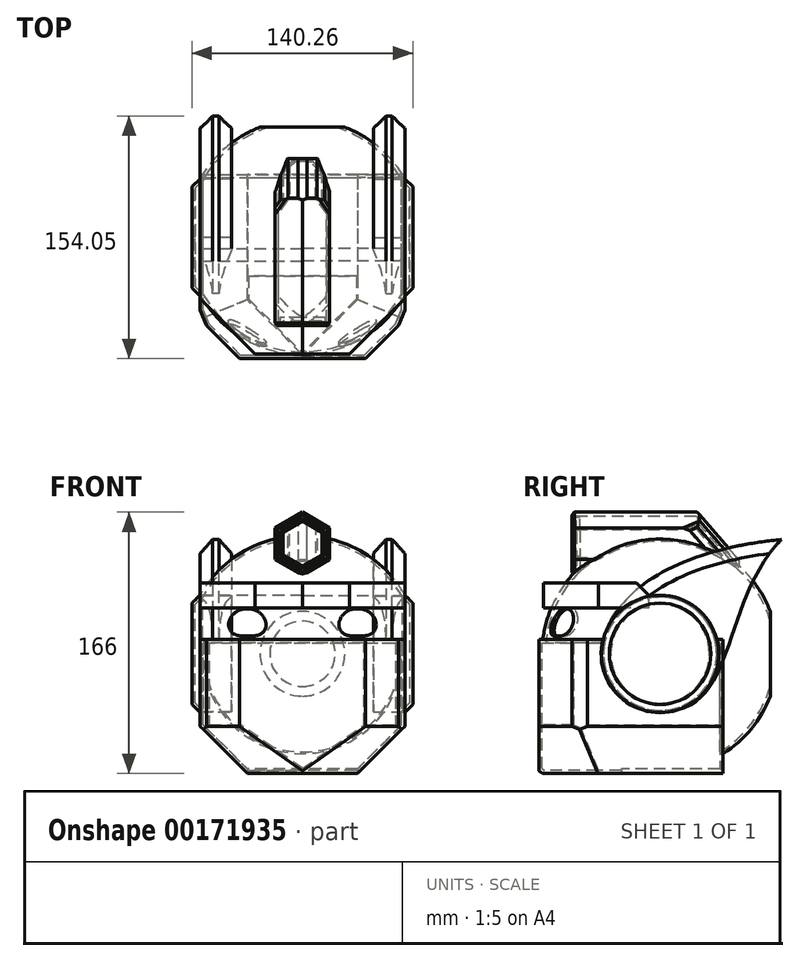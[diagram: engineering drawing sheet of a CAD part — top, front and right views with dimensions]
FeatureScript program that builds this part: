
annotation { "Feature Type Name" : "Feature", "Feature Type Description" : "" }
export const myFeature = defineFeature(function(context is Context, id is Id, definition is map)
    precondition{}
    {
        {
            var Q0;
            Q0=qCreatedBy(makeId("Top.planeOp"),FACE);
            var sketch = newSketch(context, id + "F0", { "sketchPlane" : qUnion([Q0])});
            skArc(sketch, "E0", {"start": v(0, 75) * mm, "mid": v(-75, 0) * mm, "end": v(0, -75) * mm});
            skLineSegment(sketch, "E1", {"start": v(0, 84.9) * mm, "end": v(0, -83.98) * mm});
            skSolve(sketch);
        }
        {
            var Q0;
            Q0=makeQuery(id+"F0.imprint","IMPRINT",FACE,{"disambiguationData":[TD([[makeQuery(id+"F0.imprint","IMPRINT",EDGE,{"derivedFrom":sQuery(id+"F0.wireOp",EDGE,"E0")}),1.0]])]});
            var Q1;
            Q1=sQuery(id+"F0.wireOp",EDGE,"E0");
            var Q2;
            Q2=sQuery(id+"F0.wireOp",EDGE,"E1");
            revolve(context, id + "F1", {"entities" : qUnion([Q0]), "surfaceEntities" : qUnion([Q1]), "axis" : qUnion([Q2]), "revolveType" : RevolveType.FULL});
        }
        {
            var Q0;
            Q0=qCreatedBy(makeId("Front.planeOp"),FACE);
            cPlane(context, id + "F2", {"entities" : qUnion([Q0]), "cplaneType" : CPlaneType.OFFSET, "offset" : 75 * mm, "width" : 150 * mm, "height" : 150 * mm});
        }
        {
            var Q0;
            Q0=qCreatedBy(makeId("Front.planeOp"),FACE);
            cPlane(context, id + "F3", {"entities" : qUnion([Q0]), "cplaneType" : CPlaneType.OFFSET, "offset" : 70 * mm, "oppositeDirection" : true, "width" : 150 * mm, "height" : 150 * mm});
        }
        {
            var Q0;
            Q0=qCreatedBy(id+"F3.planeOp",FACE);
            var sketch = newSketch(context, id + "F4", { "sketchPlane" : qUnion([Q0])});
            skLineSegment(sketch, "E2.bottom", {"start": v(32.42, 33.51) * mm, "end": v(-32.42, 33.51) * mm});
            skLineSegment(sketch, "E2.top", {"start": v(32.42, -33.51) * mm, "end": v(-32.42, -33.51) * mm});
            skLineSegment(sketch, "E2.left", {"start": v(32.42, 33.51) * mm, "end": v(32.42, -33.51) * mm});
            skLineSegment(sketch, "E2.right", {"start": v(-32.42, 33.51) * mm, "end": v(-32.42, -33.51) * mm});
            skPoint(sketch, "E2.middle", {"position": v(0, 0) * mm});
            skSolve(sketch);
        }
        {
            var Q0;
            Q0 = qSketchRegion(id + "F4", true);
            extrude(context, id + "F5", {"entities" : qUnion([Q0]), "operationType" : NewBodyOperationType.REMOVE, "oppositeDirection" : true, "depth" : 25 * mm});
        }
        {
            var Q0;
            Q0=qCreatedBy(id+"F2.planeOp",FACE);
            var sketch = newSketch(context, id + "F6", { "sketchPlane" : qUnion([Q0])});
            skCircle(sketch, "E3", {"center": v(-35, 20) * mm, "radius": 15 * mm});
            skLineSegment(sketch, "E4", {"start": v(-59.74, 0) * mm, "end": v(64.05, 0) * mm, "construction": true});
            skLineSegment(sketch, "E5", {"start": v(0, 51.11) * mm, "end": v(0, -49.41) * mm, "construction": true});
            skLineSegment(sketch, "E6.bottom", {"start": v(-45, 26.5) * mm, "end": v(-25, 26.5) * mm});
            skLineSegment(sketch, "E6.top", {"start": v(-45, 13.5) * mm, "end": v(-25, 13.5) * mm});
            skLineSegment(sketch, "E6.left", {"start": v(-45, 26.5) * mm, "end": v(-45, 13.5) * mm});
            skLineSegment(sketch, "E6.right", {"start": v(-25, 26.5) * mm, "end": v(-25, 13.5) * mm});
            skLineSegment(sketch, "E7.MirrorCS", {"start": v(25, 26.5) * mm, "end": v(25, 13.5) * mm});
            skLineSegment(sketch, "E8.MirrorCS", {"start": v(45, 26.5) * mm, "end": v(25, 26.5) * mm});
            skLineSegment(sketch, "E9.MirrorCS", {"start": v(45, 13.5) * mm, "end": v(25, 13.5) * mm});
            skLineSegment(sketch, "E10.MirrorCS", {"start": v(45, 26.5) * mm, "end": v(45, 13.5) * mm});
            skSolve(sketch);
        }
        {
            var Q0;
            Q0=makeQuery(id+"F6.imprint","IMPRINT",FACE,{"disambiguationData":[TD([[makeQuery(id+"F6.imprint","IMPRINT",EDGE,{"derivedFrom":sQuery(id+"F6.wireOp",EDGE,"E7.MirrorCS")}),1.0]])]});
            var Q1;
            Q1=makeQuery(id+"F6.imprint","IMPRINT",FACE,{"disambiguationData":[TD([[makeQuery(id+"F6.imprint","IMPRINT",EDGE,{"derivedFrom":sQuery(id+"F6.wireOp",EDGE,"E6.bottom")}),-1.0]])]});
            extrude(context, id + "F7", {"entities" : qUnion([Q0, Q1]), "operationType" : NewBodyOperationType.REMOVE, "oppositeDirection" : true, "depth" : 25 * mm});
        }
        {
            var Q0;
            Q0=qCreatedBy(makeId("Right.planeOp"),FACE);
            var sketch = newSketch(context, id + "F8", { "sketchPlane" : qUnion([Q0])});
            skLineSegment(sketch, "E11", {"start": v(-77, 9) * mm, "end": v(-77, -76) * mm});
            skLineSegment(sketch, "E12", {"start": v(-77, -76) * mm, "end": v(40, -76) * mm});
            skLineSegment(sketch, "E13", {"start": v(40, -76) * mm, "end": v(40, 9) * mm});
            skLineSegment(sketch, "E14", {"start": v(-77, 9) * mm, "end": v(40, 9) * mm});
            skSolve(sketch);
        }
        {
            var Q0;
            Q0 = qSketchRegion(id + "F8", true);
            extrude(context, id + "F9", {"entities" : qUnion([Q0]), "operationType" : NewBodyOperationType.ADD, "endBound" : BoundingType.SYMMETRIC, "depth" : 130 * mm});
        }
        {
            var Q0;
            Q0=qCreatedBy(makeId("Top.planeOp"),FACE);
            var sketch = newSketch(context, id + "F10", { "sketchPlane" : qUnion([Q0])});
            skLineSegment(sketch, "E15", {"start": v(0, -130) * mm, "end": v(-141.87, 0) * mm});
            skLineSegment(sketch, "E16", {"start": v(-141.87, 0) * mm, "end": v(0, 0) * mm});
            skLineSegment(sketch, "E17", {"start": v(0, 0) * mm, "end": v(0, -130) * mm});
            skLineSegment(sketch, "E18.MirrorCS", {"start": v(0, -130) * mm, "end": v(141.87, 0) * mm});
            skLineSegment(sketch, "E19.MirrorCS", {"start": v(141.87, 0) * mm, "end": v(0, 0) * mm});
            skLineSegment(sketch, "E20.bottom", {"start": v(-81.28, 0) * mm, "end": v(78.72, 0) * mm});
            skLineSegment(sketch, "E20.top", {"start": v(-81.28, -150) * mm, "end": v(78.72, -150) * mm});
            skLineSegment(sketch, "E20.left", {"start": v(-81.28, 0) * mm, "end": v(-81.28, -150) * mm});
            skLineSegment(sketch, "E20.right", {"start": v(78.72, 0) * mm, "end": v(78.72, -150) * mm});
            skLineSegment(sketch, "E21.bottom", {"start": v(-93.95, -108.92) * mm, "end": v(106.59, -108.92) * mm});
            skLineSegment(sketch, "E21.top", {"start": v(-93.95, -86.95) * mm, "end": v(106.59, -86.95) * mm});
            skLineSegment(sketch, "E21.left", {"start": v(-93.95, -108.92) * mm, "end": v(-93.95, -86.95) * mm});
            skLineSegment(sketch, "E21.right", {"start": v(106.59, -108.92) * mm, "end": v(106.59, -86.95) * mm});
            skSolve(sketch);
        }
        {
            var Q0;
            Q0=qCreatedBy(id+"F2.planeOp",FACE);
            var sketch = newSketch(context, id + "F11", { "sketchPlane" : qUnion([Q0])});
            skLineSegment(sketch, "E22.bottom", {"start": v(-79.13, 41.89) * mm, "end": v(-65.13, 41.89) * mm});
            skLineSegment(sketch, "E22.top", {"start": v(-79.13, -58.11) * mm, "end": v(-65.13, -58.11) * mm});
            skLineSegment(sketch, "E22.left", {"start": v(-79.13, 41.89) * mm, "end": v(-79.13, -58.11) * mm});
            skLineSegment(sketch, "E22.right", {"start": v(-65.13, 41.89) * mm, "end": v(-65.13, -58.11) * mm});
            skLineSegment(sketch, "E23.MirrorCS", {"start": v(65.13, 41.89) * mm, "end": v(65.13, -58.11) * mm});
            skLineSegment(sketch, "E24.MirrorCS", {"start": v(79.13, 41.89) * mm, "end": v(65.13, 41.89) * mm});
            skLineSegment(sketch, "E25.MirrorCS", {"start": v(79.13, 41.89) * mm, "end": v(79.13, -58.11) * mm});
            skLineSegment(sketch, "E26.MirrorCS", {"start": v(79.13, -58.11) * mm, "end": v(65.13, -58.11) * mm});
            skSolve(sketch);
        }
        {
            var Q0;
            Q0=makeQuery(id+"F11.imprint","IMPRINT",FACE,{"disambiguationData":[TD([[makeQuery(id+"F11.imprint","IMPRINT",EDGE,{"derivedFrom":sQuery(id+"F11.wireOp",EDGE,"E22.bottom")}),-1.0]])]});
            var Q1;
            Q1=makeQuery(id+"F11.imprint","IMPRINT",FACE,{"disambiguationData":[TD([[makeQuery(id+"F11.imprint","IMPRINT",EDGE,{"derivedFrom":sQuery(id+"F11.wireOp",EDGE,"E23.MirrorCS")}),1.0]])]});
            extrude(context, id + "F12", {"entities" : qUnion([Q0, Q1]), "operationType" : NewBodyOperationType.REMOVE, "oppositeDirection" : true, "depth" : 135.1 * mm});
        }
        {
            var Q0;
            Q0=qCreatedBy(makeId("Right.planeOp"),FACE);
            cPlane(context, id + "F13", {"entities" : qUnion([Q0]), "cplaneType" : CPlaneType.OFFSET, "offset" : 65 * mm, "width" : 150 * mm, "height" : 150 * mm});
        }
        {
            var Q0;
            {var subQ1=sQuery(id+"F10.wireOp",EDGE,"E20.top");Q0=makeQuery(id+"F10.imprint","IMPRINT",FACE,{"disambiguationData":[TD([[makeQuery(id+"F10.imprint","IMPRINT",EDGE,{"derivedFrom":subQ1}),1.0]])]});}
            extrude(context, id + "F14", {"entities" : qUnion([Q0]), "operationType" : NewBodyOperationType.REMOVE, "endBound" : BoundingType.THROUGH_ALL, "oppositeDirection" : true, "depth" : 25 * mm});
        }
        {
            var Q0;
            Q0=makeQuery(id+"F9.opExtrude","CAP_EDGE",EDGE,{"disambiguationData":[OSD([sQuery(id+"F8.wireOp",EDGE,"E11")])],"isStart":true});
            var Q1;
            Q1=makeQuery(id+"F9.opExtrude","CAP_EDGE",EDGE,{"disambiguationData":[OSD([sQuery(id+"F8.wireOp",EDGE,"E11")])],"isStart":false});
            chamfer(context, id + "F15", {"entities" : qUnion([Q0, Q1]), "width" : 25 * mm, "tangentPropagation" : true});
        }
        {
            var Q0;
            Q0=makeQuery(id+"F7.boolean.opBoolean","COPY",EDGE,{"derivedFrom":makeQuery(id+"F7.opExtrude","SWEPT_EDGE",EDGE,{"disambiguationData":[OSD([sQuery(id+"F6.wireOp",EDGE,"E7.MirrorCS"),sQuery(id+"F6.wireOp",EDGE,"E8.MirrorCS")])]})});
            var Q1;
            Q1=makeQuery(id+"F7.boolean.opBoolean","COPY",EDGE,{"derivedFrom":makeQuery(id+"F7.opExtrude","SWEPT_EDGE",EDGE,{"disambiguationData":[OSD([sQuery(id+"F6.wireOp",EDGE,"E6.bottom"),sQuery(id+"F6.wireOp",EDGE,"E6.right")])]})});
            var Q2;
            Q2=makeQuery(id+"F7.boolean.opBoolean","COPY",EDGE,{"derivedFrom":makeQuery(id+"F7.opExtrude","SWEPT_EDGE",EDGE,{"disambiguationData":[OSD([sQuery(id+"F6.wireOp",EDGE,"E6.bottom"),sQuery(id+"F6.wireOp",EDGE,"E6.left")])]})});
            var Q3;
            Q3=makeQuery(id+"F7.boolean.opBoolean","COPY",EDGE,{"derivedFrom":makeQuery(id+"F7.opExtrude","SWEPT_EDGE",EDGE,{"disambiguationData":[OSD([sQuery(id+"F6.wireOp",EDGE,"E8.MirrorCS"),sQuery(id+"F6.wireOp",EDGE,"E10.MirrorCS")])]})});
            fillet(context, id + "F16", {"entities" : qUnion([Q0, Q1, Q2, Q3]), "radius" : 9 * mm, "tangentPropagation" : true, "allowEdgeOverflow" : false});
        }
        {
            var Q0;
            Q0=makeQuery(id+"F15.opChamfer","BLEND_EDGE",EDGE,{"blendedFrom":[makeQuery(id+"F9.opExtrude","CAP_EDGE",EDGE,{"disambiguationData":[OSD([sQuery(id+"F8.wireOp",EDGE,"E11")])],"isStart":false}),makeQuery(id+"F9.opExtrude","SWEPT_FACE",FACE,{"disambiguationData":[OSD([sQuery(id+"F8.wireOp",EDGE,"E12")])]})],"blendedInto":[makeQuery(id+"F9.opExtrude","SWEPT_FACE",FACE,{"disambiguationData":[OSD([sQuery(id+"F8.wireOp",EDGE,"E12")])]})]});
            var Q1;
            Q1=makeQuery(id+"F9.opExtrude","CAP_EDGE",EDGE,{"disambiguationData":[OSD([sQuery(id+"F8.wireOp",EDGE,"E12")])],"isStart":false});
            var Q2;
            Q2=makeQuery(id+"F15.opChamfer","BLEND_EDGE",EDGE,{"blendedFrom":[makeQuery(id+"F9.opExtrude","CAP_EDGE",EDGE,{"disambiguationData":[OSD([sQuery(id+"F8.wireOp",EDGE,"E11")])],"isStart":true}),makeQuery(id+"F9.opExtrude","SWEPT_FACE",FACE,{"disambiguationData":[OSD([sQuery(id+"F8.wireOp",EDGE,"E12")])]})],"blendedInto":[makeQuery(id+"F9.opExtrude","SWEPT_FACE",FACE,{"disambiguationData":[OSD([sQuery(id+"F8.wireOp",EDGE,"E12")])]})]});
            var Q3;
            Q3=makeQuery(id+"F9.opExtrude","CAP_EDGE",EDGE,{"disambiguationData":[OSD([sQuery(id+"F8.wireOp",EDGE,"E12")])],"isStart":true});
            chamfer(context, id + "F17", {"entities" : qUnion([Q0, Q1, Q2, Q3]), "width" : 30 * mm, "tangentPropagation" : true});
        }
        {
            var Q0;
            {var subQ0=sQuery(id+"F8.wireOp",EDGE,"E11");Q0=makeQuery(id+"F15.opChamfer","BLEND_EDGE",EDGE,{"blendedFrom":[makeQuery(id+"F9.opExtrude","CAP_EDGE",EDGE,{"disambiguationData":[OSD([subQ0])],"isStart":false}),makeQuery(id+"F9.opExtrude","CAP_FACE",FACE,{"disambiguationData":[OSD([subQ0,sQuery(id+"F8.wireOp",EDGE,"E12"),sQuery(id+"F8.wireOp",EDGE,"E13"),sQuery(id+"F8.wireOp",EDGE,"E14")])],"isStart":false})],"blendedInto":[makeQuery(id+"F9.opExtrude","CAP_FACE",FACE,{"disambiguationData":[OSD([subQ0,sQuery(id+"F8.wireOp",EDGE,"E12"),sQuery(id+"F8.wireOp",EDGE,"E13"),sQuery(id+"F8.wireOp",EDGE,"E14")])],"isStart":false})]});}
            var Q1;
            {var subQ0=sQuery(id+"F8.wireOp",EDGE,"E11");Q1=makeQuery(id+"F15.opChamfer","BLEND_EDGE",EDGE,{"blendedFrom":[makeQuery(id+"F9.opExtrude","CAP_EDGE",EDGE,{"disambiguationData":[OSD([subQ0])],"isStart":true}),makeQuery(id+"F9.opExtrude","CAP_FACE",FACE,{"disambiguationData":[OSD([subQ0,sQuery(id+"F8.wireOp",EDGE,"E12"),sQuery(id+"F8.wireOp",EDGE,"E13"),sQuery(id+"F8.wireOp",EDGE,"E14")])],"isStart":true})],"blendedInto":[makeQuery(id+"F9.opExtrude","CAP_FACE",FACE,{"disambiguationData":[OSD([subQ0,sQuery(id+"F8.wireOp",EDGE,"E12"),sQuery(id+"F8.wireOp",EDGE,"E13"),sQuery(id+"F8.wireOp",EDGE,"E14")])],"isStart":true})]});}
            chamfer(context, id + "F18", {"entities" : qUnion([Q0, Q1]), "width" : 14 * mm, "tangentPropagation" : true});
        }
        {
            var Q0;
            Q0=qCreatedBy(id+"F13.planeOp",FACE);
            var sketch = newSketch(context, id + "F19", { "sketchPlane" : qUnion([Q0])});
            skCircle(sketch, "E27", {"center": v(0, 0) * mm, "radius": 36.9 * mm});
            skFitSpline(sketch, "E28", {"points": [v(-35.7, 9.3) * mm, v(77.05, 72.6) * mm], "startDerivative": vector(24.7, 96.57) * mm, "endDerivative": vector(194.9, 19.2) * mm});
            skFitSpline(sketch, "E29", {"points": [v(77.05, 72.6) * mm, v(0, -36.9) * mm], "startDerivative": vector(-117.67, -120.6) * mm, "endDerivative": vector(-149.2, 2.86) * mm});
            skSolve(sketch);
        }
        {
            var Q0;
            {var subQ0=sQuery(id+"F19.wireOp",EDGE,"E28");Q0=makeQuery(id+"F19.imprint","IMPRINT",FACE,{"disambiguationData":[TD([[makeQuery(id+"F19.imprint","IMPRINT",EDGE,{"derivedFrom":subQ0}),-1.0]])]});}
            var Q1;
            Q1=makeQuery(id+"F12.boolean.opBoolean","COPY",FACE,{"derivedFrom":makeQuery(id+"F12.opExtrude","SWEPT_FACE",FACE,{"disambiguationData":[OSD([sQuery(id+"F11.wireOp",EDGE,"E23.MirrorCS")])]})});
            extrude(context, id + "F20", {"entities" : qUnion([Q0, Q1]), "oppositeDirection" : true, "depth" : 20 * mm});
        }
        {
            var Q0;
            Q0=makeQuery(id+"F20.opExtrude","SWEPT_BODY",BODY,{"disambiguationData":[OSD([sQuery(id+"F19.wireOp",EDGE,"E27"),sQuery(id+"F19.wireOp",EDGE,"E28"),sQuery(id+"F19.wireOp",EDGE,"E29")])]});
            var Q1;
            Q1=qCreatedBy(makeId("Right.planeOp"),FACE);
            mirror(context, id + "F21", {"entities" : qUnion([Q0]), "mirrorPlane" : qUnion([Q1])});
        }
        {
            var Q0;
            Q0=makeQuery(id+"F12.boolean.opBoolean","COPY",FACE,{"derivedFrom":makeQuery(id+"F12.opExtrude","SWEPT_FACE",FACE,{"disambiguationData":[OSD([sQuery(id+"F11.wireOp",EDGE,"E23.MirrorCS")])]})});
            extrude(context, id + "F22", {"entities" : qUnion([Q0]), "depth" : 5 * mm});
        }
        {
            var Q0;
            Q0=makeQuery(id+"F22.opExtrude","CAP_EDGE",EDGE,{"disambiguationData":[OSD([sQuery(id+"F0.wireOp",EDGE,"E0"),sQuery(id+"F11.wireOp",EDGE,"E23.MirrorCS")])],"isStart":false});
            chamfer(context, id + "F23", {"entities" : qUnion([Q0]), "width" : 5 * mm, "tangentPropagation" : true});
        }
        {
            var Q0;
            Q0=makeQuery(id+"F22.opExtrude","SWEPT_BODY",BODY,{"disambiguationData":[OSD([sQuery(id+"F11.wireOp",EDGE,"E23.MirrorCS")])]});
            var Q1;
            Q1=qCreatedBy(makeId("Right.planeOp"),FACE);
            mirror(context, id + "F24", {"operationType" : NewBodyOperationType.ADD, "entities" : qUnion([Q0]), "mirrorPlane" : qUnion([Q1])});
        }
        {
            var Q0;
            Q0=makeQuery(id+"F20.opExtrude","CAP_EDGE",EDGE,{"disambiguationData":[OSD([sQuery(id+"F19.wireOp",EDGE,"E28")])],"isStart":false});
            var Q1;
            Q1=makeQuery(id+"F21.opPattern","COPY",EDGE,{"derivedFrom":makeQuery(id+"F20.opExtrude","CAP_EDGE",EDGE,{"disambiguationData":[OSD([sQuery(id+"F19.wireOp",EDGE,"E28")])],"isStart":false}),"instanceName":"1"});
            var Q2;
            Q2=makeQuery(id+"F21.opPattern","COPY",EDGE,{"derivedFrom":makeQuery(id+"F20.opExtrude","CAP_EDGE",EDGE,{"disambiguationData":[OSD([sQuery(id+"F19.wireOp",EDGE,"E28")])],"isStart":true}),"instanceName":"1"});
            var Q3;
            Q3=makeQuery(id+"F20.opExtrude","CAP_EDGE",EDGE,{"disambiguationData":[OSD([sQuery(id+"F19.wireOp",EDGE,"E28")])],"isStart":true});
            chamfer(context, id + "F25", {"entities" : qUnion([Q0, Q1, Q2, Q3]), "width" : 8 * mm, "tangentPropagation" : true});
        }
        {
            var Q0;
            Q0=qCreatedBy(makeId("Right.planeOp"),FACE);
            var sketch = newSketch(context, id + "F26", { "sketchPlane" : qUnion([Q0])});
            skLineSegment(sketch, "E30.bottom", {"start": v(-7, 29) * mm, "end": v(-74, 29) * mm});
            skLineSegment(sketch, "E30.top", {"start": v(-7, 45) * mm, "end": v(-74, 45) * mm});
            skLineSegment(sketch, "E30.left", {"start": v(-7, 29) * mm, "end": v(-7, 45) * mm});
            skLineSegment(sketch, "E30.right", {"start": v(-74, 29) * mm, "end": v(-74, 45) * mm});
            skSolve(sketch);
        }
        {
            var Q0;
            Q0 = qSketchRegion(id + "F26", true);
            var Q1;
            Q1=makeQuery(id+"F20.opExtrude","SWEPT_BODY",BODY,{"disambiguationData":[OSD([sQuery(id+"F11.wireOp",EDGE,"E23.MirrorCS")])]});
            extrude(context, id + "F27", {"entities" : qUnion([Q0]), "endBoundEntityBody" : qUnion([Q1]), "depth" : 65 * mm});
        }
        {
            var Q0;
            Q0=makeQuery(id+"F27.opExtrude","CAP_EDGE",EDGE,{"disambiguationData":[OSD([sQuery(id+"F26.wireOp",EDGE,"E30.right")])],"isStart":false});
            chamfer(context, id + "F28", {"entities" : qUnion([Q0]), "width" : 35 * mm, "tangentPropagation" : true});
        }
        {
            var Q0;
            Q0=makeQuery(id+"F27.opExtrude","SWEPT_EDGE",EDGE,{"disambiguationData":[OSD([sQuery(id+"F26.wireOp",EDGE,"E30.top"),sQuery(id+"F26.wireOp",EDGE,"E30.left")])]});
            chamfer(context, id + "F29", {"entities" : qUnion([Q0]), "width" : 8 * mm, "tangentPropagation" : true});
        }
        {
            var Q0;
            Q0=makeQuery(id+"F27.opExtrude","SWEPT_BODY",BODY,{"disambiguationData":[OSD([sQuery(id+"F26.wireOp",EDGE,"E30.bottom"),sQuery(id+"F26.wireOp",EDGE,"E30.top"),sQuery(id+"F26.wireOp",EDGE,"E30.left"),sQuery(id+"F26.wireOp",EDGE,"E30.right")])]});
            var Q1;
            Q1=qCreatedBy(makeId("Right.planeOp"),FACE);
            mirror(context, id + "F30", {"entities" : qUnion([Q0]), "mirrorPlane" : qUnion([Q1])});
        }
        {
            var Q0;
            Q0=qCreatedBy(makeId("Front.planeOp"),FACE);
            var sketch = newSketch(context, id + "F31", { "sketchPlane" : qUnion([Q0])});
            skCircle(sketch, "E31.cCircle", {"center": v(0, 70) * mm, "radius": 20 * mm, "construction": true});
            skLineSegment(sketch, "E31.0", {"start": v(0, 90) * mm, "end": v(17.32, 80) * mm});
            skLineSegment(sketch, "E31.1", {"start": v(17.32, 80) * mm, "end": v(17.32, 60) * mm});
            skLineSegment(sketch, "E31.2", {"start": v(17.32, 60) * mm, "end": v(0, 50) * mm});
            skLineSegment(sketch, "E31.3", {"start": v(0, 50) * mm, "end": v(-17.32, 60) * mm});
            skLineSegment(sketch, "E31.4", {"start": v(-17.32, 60) * mm, "end": v(-17.32, 80) * mm});
            skLineSegment(sketch, "E31.5", {"start": v(-17.32, 80) * mm, "end": v(0, 90) * mm});
            skSolve(sketch);
        }
        {
            var Q0;
            Q0 = qSketchRegion(id + "F31", true);
            extrude(context, id + "F32", {"entities" : qUnion([Q0]), "operationType" : NewBodyOperationType.ADD, "depth" : 56 * mm});
        }
        {
            var Q0;
            Q0 = qSketchRegion(id + "F31", true);
            extrude(context, id + "F33", {"entities" : qUnion([Q0]), "operationType" : NewBodyOperationType.ADD, "oppositeDirection" : true, "depth" : 50 * mm});
        }
        {
            var Q0;
            Q0=makeQuery(id+"F33.opExtrude","CAP_EDGE",EDGE,{"disambiguationData":[OSD([sQuery(id+"F31.wireOp",EDGE,"E31.0")])],"isStart":false});
            var Q1;
            Q1=makeQuery(id+"F33.opExtrude","CAP_EDGE",EDGE,{"disambiguationData":[OSD([sQuery(id+"F31.wireOp",EDGE,"E31.5")])],"isStart":false});
            chamfer(context, id + "F34", {"entities" : qUnion([Q0, Q1]), "width" : 25 * mm, "tangentPropagation" : true});
        }
        {
            var Q0;
            Q0=makeQuery(id+"F32.opExtrude","CAP_FACE",FACE,{"disambiguationData":[OSD([sQuery(id+"F31.wireOp",EDGE,"E31.0"),sQuery(id+"F31.wireOp",EDGE,"E31.1"),sQuery(id+"F31.wireOp",EDGE,"E31.2"),sQuery(id+"F31.wireOp",EDGE,"E31.3"),sQuery(id+"F31.wireOp",EDGE,"E31.4"),sQuery(id+"F31.wireOp",EDGE,"E31.5")])],"isStart":false});
            var sketch = newSketch(context, id + "F35", { "sketchPlane" : qUnion([Q0])});
            skLineSegment(sketch, "E32.0", {"start": v(12.32, 77.11) * mm, "end": v(0, 84.23) * mm});
            skLineSegment(sketch, "E32.1", {"start": v(-12.32, 77.11) * mm, "end": v(-12.32, 62.89) * mm});
            skLineSegment(sketch, "E32.2", {"start": v(-12.32, 62.89) * mm, "end": v(0, 55.77) * mm});
            skLineSegment(sketch, "E32.3", {"start": v(0, 84.23) * mm, "end": v(-12.32, 77.11) * mm});
            skLineSegment(sketch, "E32.4", {"start": v(0, 55.77) * mm, "end": v(12.32, 62.89) * mm});
            skLineSegment(sketch, "E32.5", {"start": v(12.32, 62.89) * mm, "end": v(12.32, 77.11) * mm});
            skSolve(sketch);
        }
        {
            var Q0;
            Q0 = qSketchRegion(id + "F35", true);
            extrude(context, id + "F36", {"entities" : qUnion([Q0]), "operationType" : NewBodyOperationType.REMOVE, "oppositeDirection" : true, "depth" : 3 * mm});
        }
        {
            var Q0;
            Q0=makeQuery(id+"F32.opExtrude","CAP_FACE",FACE,{"disambiguationData":[OSD([sQuery(id+"F31.wireOp",EDGE,"E31.0"),sQuery(id+"F31.wireOp",EDGE,"E31.1"),sQuery(id+"F31.wireOp",EDGE,"E31.2"),sQuery(id+"F31.wireOp",EDGE,"E31.3"),sQuery(id+"F31.wireOp",EDGE,"E31.4"),sQuery(id+"F31.wireOp",EDGE,"E31.5")])],"isStart":false});
            chamfer(context, id + "F37", {"entities" : qUnion([Q0]), "width" : 1.5 * mm, "tangentPropagation" : true});
        }
        {
            var Q0;
            {var subQ0=sQuery(id+"F31.wireOp",EDGE,"E31.4");Q0=makeQuery(id+"F34.opChamfer","BLEND_EDGE",EDGE,{"blendedFrom":[makeQuery(id+"F33.opExtrude","CAP_EDGE",EDGE,{"disambiguationData":[OSD([sQuery(id+"F31.wireOp",EDGE,"E31.5")])],"isStart":false}),makeQuery(id+"F33.boolean.opBoolean","MERGE",FACE,{"derivedFrom":[makeQuery(id+"F32.opExtrude","SWEPT_FACE",FACE,{"disambiguationData":[OSD([subQ0])]}),makeQuery(id+"F33.opExtrude","SWEPT_FACE",FACE,{"disambiguationData":[OSD([subQ0])]})]})],"blendedInto":[makeQuery(id+"F33.boolean.opBoolean","MERGE",FACE,{"derivedFrom":[makeQuery(id+"F32.opExtrude","SWEPT_FACE",FACE,{"disambiguationData":[OSD([subQ0])]}),makeQuery(id+"F33.opExtrude","SWEPT_FACE",FACE,{"disambiguationData":[OSD([subQ0])]})]})]});}
            var Q1;
            {var subQ0=sQuery(id+"F31.wireOp",EDGE,"E31.1");Q1=makeQuery(id+"F34.opChamfer","BLEND_EDGE",EDGE,{"blendedFrom":[makeQuery(id+"F33.opExtrude","CAP_EDGE",EDGE,{"disambiguationData":[OSD([sQuery(id+"F31.wireOp",EDGE,"E31.0")])],"isStart":false}),makeQuery(id+"F33.boolean.opBoolean","MERGE",FACE,{"derivedFrom":[makeQuery(id+"F32.opExtrude","SWEPT_FACE",FACE,{"disambiguationData":[OSD([subQ0])]}),makeQuery(id+"F33.opExtrude","SWEPT_FACE",FACE,{"disambiguationData":[OSD([subQ0])]})]})],"blendedInto":[makeQuery(id+"F33.boolean.opBoolean","MERGE",FACE,{"derivedFrom":[makeQuery(id+"F32.opExtrude","SWEPT_FACE",FACE,{"disambiguationData":[OSD([subQ0])]}),makeQuery(id+"F33.opExtrude","SWEPT_FACE",FACE,{"disambiguationData":[OSD([subQ0])]})]})]});}
            var Q2;
            Q2=makeQuery(id+"F34.opChamfer","BLEND_EDGE",EDGE,{"blendedFrom":[makeQuery(id+"F33.opExtrude","CAP_EDGE",EDGE,{"disambiguationData":[OSD([sQuery(id+"F31.wireOp",EDGE,"E31.0")])],"isStart":false}),makeQuery(id+"F33.opExtrude","CAP_EDGE",EDGE,{"disambiguationData":[OSD([sQuery(id+"F31.wireOp",EDGE,"E31.5")])],"isStart":false})],"blendedInto":[]});
            chamfer(context, id + "F38", {"entities" : qUnion([Q0, Q1, Q2]), "width" : 8 * mm, "tangentPropagation" : true});
        }
        {
            var Q0;
            Q0=makeQuery(id+"F7.boolean.opBoolean","COPY",EDGE,{"derivedFrom":makeQuery(id+"F7.opExtrude","SWEPT_EDGE",EDGE,{"disambiguationData":[OSD([sQuery(id+"F6.wireOp",EDGE,"E6.top"),sQuery(id+"F6.wireOp",EDGE,"E6.left")])]})});
            var Q1;
            Q1=makeQuery(id+"F7.boolean.opBoolean","COPY",EDGE,{"derivedFrom":makeQuery(id+"F7.opExtrude","SWEPT_EDGE",EDGE,{"disambiguationData":[OSD([sQuery(id+"F6.wireOp",EDGE,"E9.MirrorCS"),sQuery(id+"F6.wireOp",EDGE,"E10.MirrorCS")])]})});
            fillet(context, id + "F39", {"entities" : qUnion([Q0, Q1]), "radius" : 5 * mm, "tangentPropagation" : true, "allowEdgeOverflow" : false});
        }
        {
            var Q0;
            Q0=makeQuery(id+"F7.boolean.opBoolean","COPY",EDGE,{"derivedFrom":makeQuery(id+"F7.opExtrude","SWEPT_EDGE",EDGE,{"disambiguationData":[OSD([sQuery(id+"F6.wireOp",EDGE,"E6.top"),sQuery(id+"F6.wireOp",EDGE,"E6.right")])]})});
            var Q1;
            Q1=makeQuery(id+"F7.boolean.opBoolean","COPY",EDGE,{"derivedFrom":makeQuery(id+"F7.opExtrude","SWEPT_EDGE",EDGE,{"disambiguationData":[OSD([sQuery(id+"F6.wireOp",EDGE,"E7.MirrorCS"),sQuery(id+"F6.wireOp",EDGE,"E9.MirrorCS")])]})});
            fillet(context, id + "F40", {"entities" : qUnion([Q0, Q1]), "radius" : 5 * mm, "tangentPropagation" : true, "allowEdgeOverflow" : false});
        }
        {
            var Q0;
            {var subQ0=sQuery(id+"F31.wireOp",EDGE,"E31.5");var subQ1=sQuery(id+"F31.wireOp",EDGE,"E31.4");Q0=makeQuery(id+"F38.opChamfer","BLEND_EDGE",EDGE,{"blendedFrom":[makeQuery(id+"F34.opChamfer","BLEND_EDGE",EDGE,{"blendedFrom":[makeQuery(id+"F33.opExtrude","CAP_EDGE",EDGE,{"disambiguationData":[OSD([subQ0])],"isStart":false}),makeQuery(id+"F33.boolean.opBoolean","MERGE",FACE,{"derivedFrom":[makeQuery(id+"F32.opExtrude","SWEPT_FACE",FACE,{"disambiguationData":[OSD([subQ1])]}),makeQuery(id+"F33.opExtrude","SWEPT_FACE",FACE,{"disambiguationData":[OSD([subQ1])]})]})],"blendedInto":[makeQuery(id+"F33.boolean.opBoolean","MERGE",FACE,{"derivedFrom":[makeQuery(id+"F32.opExtrude","SWEPT_FACE",FACE,{"disambiguationData":[OSD([subQ1])]}),makeQuery(id+"F33.opExtrude","SWEPT_FACE",FACE,{"disambiguationData":[OSD([subQ1])]})]})]}),makeQuery(id+"F33.boolean.opBoolean","MERGE",FACE,{"derivedFrom":[makeQuery(id+"F32.opExtrude","SWEPT_FACE",FACE,{"disambiguationData":[OSD([subQ0])]}),makeQuery(id+"F33.opExtrude","SWEPT_FACE",FACE,{"disambiguationData":[OSD([subQ0])]})]})],"blendedInto":[makeQuery(id+"F33.boolean.opBoolean","MERGE",FACE,{"derivedFrom":[makeQuery(id+"F32.opExtrude","SWEPT_FACE",FACE,{"disambiguationData":[OSD([subQ0])]}),makeQuery(id+"F33.opExtrude","SWEPT_FACE",FACE,{"disambiguationData":[OSD([subQ0])]})]})]});}
            var Q1;
            {var subQ0=sQuery(id+"F31.wireOp",EDGE,"E31.0");var subQ1=sQuery(id+"F31.wireOp",EDGE,"E31.1");Q1=makeQuery(id+"F38.opChamfer","BLEND_EDGE",EDGE,{"blendedFrom":[makeQuery(id+"F34.opChamfer","BLEND_EDGE",EDGE,{"blendedFrom":[makeQuery(id+"F33.opExtrude","CAP_EDGE",EDGE,{"disambiguationData":[OSD([subQ0])],"isStart":false}),makeQuery(id+"F33.boolean.opBoolean","MERGE",FACE,{"derivedFrom":[makeQuery(id+"F32.opExtrude","SWEPT_FACE",FACE,{"disambiguationData":[OSD([subQ1])]}),makeQuery(id+"F33.opExtrude","SWEPT_FACE",FACE,{"disambiguationData":[OSD([subQ1])]})]})],"blendedInto":[makeQuery(id+"F33.boolean.opBoolean","MERGE",FACE,{"derivedFrom":[makeQuery(id+"F32.opExtrude","SWEPT_FACE",FACE,{"disambiguationData":[OSD([subQ1])]}),makeQuery(id+"F33.opExtrude","SWEPT_FACE",FACE,{"disambiguationData":[OSD([subQ1])]})]})]}),makeQuery(id+"F33.boolean.opBoolean","MERGE",FACE,{"derivedFrom":[makeQuery(id+"F32.opExtrude","SWEPT_FACE",FACE,{"disambiguationData":[OSD([subQ0])]}),makeQuery(id+"F33.opExtrude","SWEPT_FACE",FACE,{"disambiguationData":[OSD([subQ0])]})]})],"blendedInto":[makeQuery(id+"F33.boolean.opBoolean","MERGE",FACE,{"derivedFrom":[makeQuery(id+"F32.opExtrude","SWEPT_FACE",FACE,{"disambiguationData":[OSD([subQ0])]}),makeQuery(id+"F33.opExtrude","SWEPT_FACE",FACE,{"disambiguationData":[OSD([subQ0])]})]})]});}
            chamfer(context, id + "F41", {"entities" : qUnion([Q0, Q1]), "width" : 5 * mm, "tangentPropagation" : true});
        }
        {
            var Q0;
            {var subQ0=sQuery(id+"F31.wireOp",EDGE,"E31.0");var subQ1=sQuery(id+"F31.wireOp",EDGE,"E31.1");Q0=makeQuery(id+"F38.opChamfer","BLEND_EDGE",EDGE,{"blendedFrom":[makeQuery(id+"F34.opChamfer","BLEND_EDGE",EDGE,{"blendedFrom":[makeQuery(id+"F33.opExtrude","CAP_EDGE",EDGE,{"disambiguationData":[OSD([subQ0])],"isStart":false}),makeQuery(id+"F33.boolean.opBoolean","MERGE",FACE,{"derivedFrom":[makeQuery(id+"F32.opExtrude","SWEPT_FACE",FACE,{"disambiguationData":[OSD([subQ1])]}),makeQuery(id+"F33.opExtrude","SWEPT_FACE",FACE,{"disambiguationData":[OSD([subQ1])]})]})],"blendedInto":[makeQuery(id+"F33.boolean.opBoolean","MERGE",FACE,{"derivedFrom":[makeQuery(id+"F32.opExtrude","SWEPT_FACE",FACE,{"disambiguationData":[OSD([subQ1])]}),makeQuery(id+"F33.opExtrude","SWEPT_FACE",FACE,{"disambiguationData":[OSD([subQ1])]})]})]}),makeQuery(id+"F34.opChamfer","BLEND_FACE",FACE,{"disambiguationData":[OSD([subQ0])]})],"blendedInto":[makeQuery(id+"F34.opChamfer","BLEND_FACE",FACE,{"disambiguationData":[OSD([subQ0])]})]});}
            var Q1;
            {var subQ0=sQuery(id+"F31.wireOp",EDGE,"E31.5");var subQ1=sQuery(id+"F31.wireOp",EDGE,"E31.4");Q1=makeQuery(id+"F38.opChamfer","BLEND_EDGE",EDGE,{"blendedFrom":[makeQuery(id+"F34.opChamfer","BLEND_EDGE",EDGE,{"blendedFrom":[makeQuery(id+"F33.opExtrude","CAP_EDGE",EDGE,{"disambiguationData":[OSD([subQ0])],"isStart":false}),makeQuery(id+"F33.boolean.opBoolean","MERGE",FACE,{"derivedFrom":[makeQuery(id+"F32.opExtrude","SWEPT_FACE",FACE,{"disambiguationData":[OSD([subQ1])]}),makeQuery(id+"F33.opExtrude","SWEPT_FACE",FACE,{"disambiguationData":[OSD([subQ1])]})]})],"blendedInto":[makeQuery(id+"F33.boolean.opBoolean","MERGE",FACE,{"derivedFrom":[makeQuery(id+"F32.opExtrude","SWEPT_FACE",FACE,{"disambiguationData":[OSD([subQ1])]}),makeQuery(id+"F33.opExtrude","SWEPT_FACE",FACE,{"disambiguationData":[OSD([subQ1])]})]})]}),makeQuery(id+"F34.opChamfer","BLEND_FACE",FACE,{"disambiguationData":[OSD([subQ0])]})],"blendedInto":[makeQuery(id+"F34.opChamfer","BLEND_FACE",FACE,{"disambiguationData":[OSD([subQ0])]})]});}
            chamfer(context, id + "F42", {"entities" : qUnion([Q0, Q1]), "width" : 10 * mm, "tangentPropagation" : true});
        }
        {
            var Q0;
            Q0=makeQuery(id+"F5.boolean.opBoolean","COPY",FACE,{"derivedFrom":makeQuery(id+"F5.opExtrude","CAP_FACE",FACE,{"disambiguationData":[OSD([sQuery(id+"F4.wireOp",EDGE,"E2.bottom"),sQuery(id+"F4.wireOp",EDGE,"E2.top"),sQuery(id+"F4.wireOp",EDGE,"E2.left"),sQuery(id+"F4.wireOp",EDGE,"E2.right")])],"isStart":true})});
            shell(context, id + "F43", {"entities" : qUnion([Q0]), "thickness" : 2 * mm});
        }
        {
            var Q0;
            Q0=makeQuery(id+"F9.opExtrude","SWEPT_FACE",FACE,{"disambiguationData":[OSD([sQuery(id+"F8.wireOp",EDGE,"E12")])]});
            var sketch = newSketch(context, id + "F44", { "sketchPlane" : qUnion([Q0])});
            skLineSegment(sketch, "E33.bottom", {"start": v(-35, -24.67) * mm, "end": v(35, -24.67) * mm});
            skLineSegment(sketch, "E33.top", {"start": v(-35, 24.67) * mm, "end": v(35, 24.67) * mm});
            skLineSegment(sketch, "E33.left", {"start": v(-35, -24.67) * mm, "end": v(-35, 24.67) * mm});
            skLineSegment(sketch, "E33.right", {"start": v(35, -24.67) * mm, "end": v(35, 24.67) * mm});
            skPoint(sketch, "E33.middle", {"position": v(0, 0) * mm});
            skLineSegment(sketch, "E34.top", {"start": v(-35, -40) * mm, "end": v(35, -40) * mm});
            skLineSegment(sketch, "E34.left", {"start": v(-35, -24.67) * mm, "end": v(-35, -40) * mm});
            skLineSegment(sketch, "E34.right", {"start": v(35, -24.67) * mm, "end": v(35, -40) * mm});
            skSolve(sketch);
        }
        {
            var Q0;
            Q0=makeQuery(id+"F44.imprint","IMPRINT",FACE,{"disambiguationData":[TD([[makeQuery(id+"F44.imprint","IMPRINT",EDGE,{"derivedFrom":sQuery(id+"F44.wireOp",EDGE,"E33.top")}),-1.0]])]});
            var Q1;
            Q1=makeQuery(id+"F44.imprint","IMPRINT",FACE,{"disambiguationData":[TD([[makeQuery(id+"F44.imprint","IMPRINT",EDGE,{"derivedFrom":sQuery(id+"F44.wireOp",EDGE,"E33.bottom")}),-1.0]])]});
            extrude(context, id + "F45", {"entities" : qUnion([Q0, Q1]), "operationType" : NewBodyOperationType.REMOVE, "oppositeDirection" : true, "depth" : 3 * mm});
        }
        {
            var Q0;
            Q0=makeQuery(id+"F43.opShell","OFFSET_FACE",FACE,{"disambiguationData":[OSD([sQuery(id+"F6.wireOp",EDGE,"E7.MirrorCS"),sQuery(id+"F6.wireOp",EDGE,"E8.MirrorCS"),sQuery(id+"F6.wireOp",EDGE,"E9.MirrorCS"),sQuery(id+"F6.wireOp",EDGE,"E10.MirrorCS")])]});
            var Q1;
            Q1=makeQuery(id+"F43.opShell","OFFSET_FACE",FACE,{"disambiguationData":[OSD([sQuery(id+"F6.wireOp",EDGE,"E6.bottom"),sQuery(id+"F6.wireOp",EDGE,"E6.top"),sQuery(id+"F6.wireOp",EDGE,"E6.left"),sQuery(id+"F6.wireOp",EDGE,"E6.right")])]});
            extrude(context, id + "F46", {"entities" : qUnion([Q0, Q1]), "operationType" : NewBodyOperationType.REMOVE, "oppositeDirection" : true, "depth" : 25 * mm});
        }
    });
